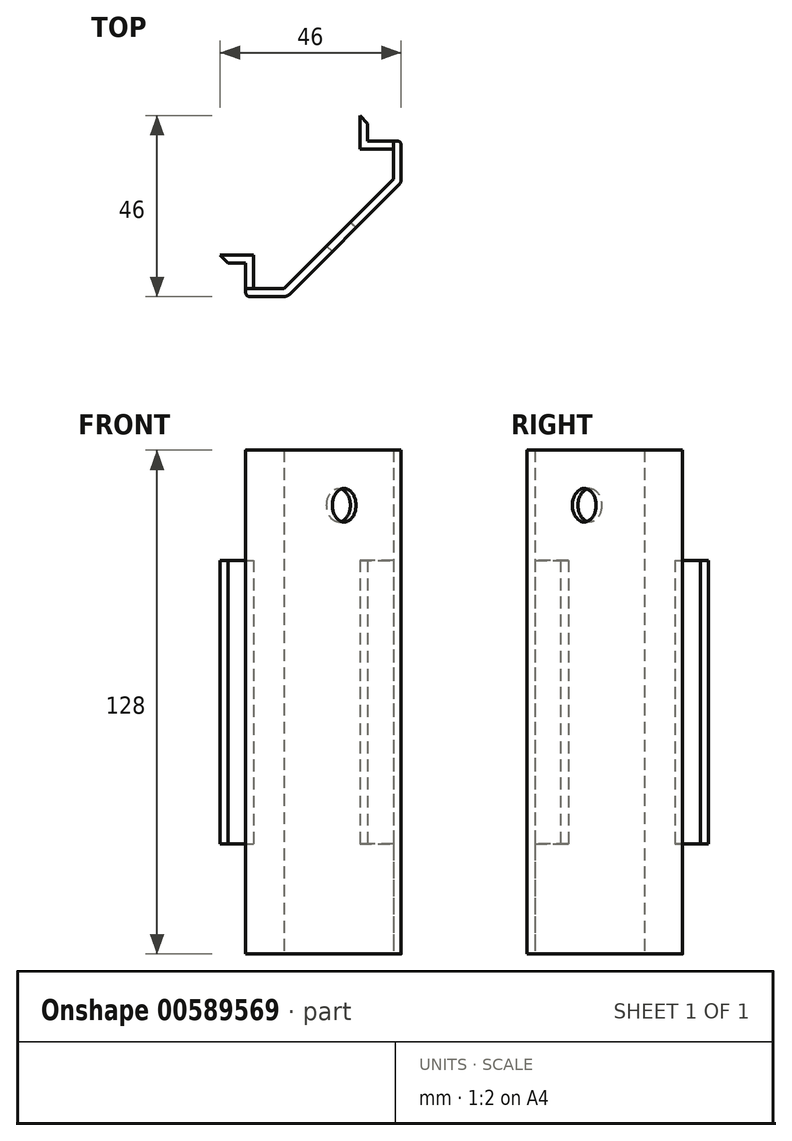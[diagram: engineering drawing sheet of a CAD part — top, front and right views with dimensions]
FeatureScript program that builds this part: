
annotation { "Feature Type Name" : "Feature", "Feature Type Description" : "" }
export const myFeature = defineFeature(function(context is Context, id is Id, definition is map)
    precondition{}
    {
        {
            var Q0;
            Q0=qCreatedBy(makeId("Top.planeOp"),FACE);
            var sketch = newSketch(context, id + "F0", { "sketchPlane" : qUnion([Q0])});
            skLineSegment(sketch, "E0", {"start": v(-68.1, 0) * mm, "end": v(72.16, 0) * mm, "construction": true});
            skLineSegment(sketch, "E1", {"start": v(0, 70.28) * mm, "end": v(0, -61.88) * mm, "construction": true});
            skLineSegment(sketch, "E2.bottom", {"start": v(-19.75, 19.75) * mm, "end": v(19.75, 19.75) * mm, "construction": true});
            skLineSegment(sketch, "E2.top", {"start": v(-19.75, -19.75) * mm, "end": v(19.75, -19.75) * mm, "construction": true});
            skLineSegment(sketch, "E2.left", {"start": v(-19.75, 19.75) * mm, "end": v(-19.75, -19.75) * mm, "construction": true});
            skLineSegment(sketch, "E2.right", {"start": v(19.75, 19.75) * mm, "end": v(19.75, -19.75) * mm, "construction": true});
            skLineSegment(sketch, "E3", {"start": v(-19.75, -19.75) * mm, "end": v(-9.25, -19.75) * mm});
            skLineSegment(sketch, "E4", {"start": v(19.75, 19.75) * mm, "end": v(19.75, 9.25) * mm});
            skLineSegment(sketch, "E5", {"start": v(-9.25, -19.75) * mm, "end": v(19.75, 9.25) * mm});
            skLineSegment(sketch, "E6.0", {"start": v(-19.75, -17.75) * mm, "end": v(-10.08, -17.75) * mm});
            skLineSegment(sketch, "E6.1", {"start": v(-10.08, -17.75) * mm, "end": v(17.75, 10.08) * mm});
            skLineSegment(sketch, "E6.2", {"start": v(17.75, 19.75) * mm, "end": v(17.75, 10.08) * mm});
            skLineSegment(sketch, "E7", {"start": v(-19.75, -19.75) * mm, "end": v(-19.75, -17.75) * mm});
            skLineSegment(sketch, "E8", {"start": v(19.75, 19.75) * mm, "end": v(17.75, 19.75) * mm});
            skSolve(sketch);
        }
        {
            var Q0;
            Q0=qSketchRegion(id+"F0",true);
            extrude(context, id + "F1", {"entities" : qUnion([Q0]), "depth" : 28 * mm, "offsetDistance" : 25 * mm});
        }
        {
            var Q0;
            Q0=makeQuery(id+"F1.opExtrude","CAP_FACE",FACE,{"disambiguationData":[OSD([sQuery(id+"F0.wireOp",EDGE,"E3"),sQuery(id+"F0.wireOp",EDGE,"E4"),sQuery(id+"F0.wireOp",EDGE,"E5"),sQuery(id+"F0.wireOp",EDGE,"E6.0"),sQuery(id+"F0.wireOp",EDGE,"E6.1"),sQuery(id+"F0.wireOp",EDGE,"E6.2"),sQuery(id+"F0.wireOp",EDGE,"E7"),sQuery(id+"F0.wireOp",EDGE,"E8")])],"isStart":false});
            var sketch = newSketch(context, id + "F2", { "sketchPlane" : qUnion([Q0])});
            skLineSegment(sketch, "E9.1", {"start": v(-9.25, -19.75) * mm, "end": v(19.75, 9.25) * mm});
            skLineSegment(sketch, "E9.2", {"start": v(19.75, 19.75) * mm, "end": v(19.75, 9.25) * mm});
            skLineSegment(sketch, "E10", {"start": v(19.75, 19.75) * mm, "end": v(11.25, 19.75) * mm});
            skLineSegment(sketch, "E11", {"start": v(17.75, 17.75) * mm, "end": v(17.75, 10.08) * mm});
            skLineSegment(sketch, "E12", {"start": v(17.75, 10.08) * mm, "end": v(16.59, 8.91) * mm});
            skLineSegment(sketch, "E13.left", {"start": v(11.25, 19.75) * mm, "end": v(11.25, 24.25) * mm});
            skLineSegment(sketch, "E14", {"start": v(11.25, 24.25) * mm, "end": v(9.25, 26.25) * mm});
            skLineSegment(sketch, "E15.trimOffspring", {"start": v(16.59, 8.91) * mm, "end": v(-8.91, -16.59) * mm});
            skLineSegment(sketch, "E16.0", {"start": v(9.25, 19.75) * mm, "end": v(9.25, 23.42) * mm});
            skLineSegment(sketch, "E17.0", {"start": v(9.25, 23.42) * mm, "end": v(9.25, 23.42) * mm});
            skLineSegment(sketch, "E18.trimOffspring", {"start": v(9.25, 23.42) * mm, "end": v(9.25, 26.25) * mm});
            skLineSegment(sketch, "E19", {"start": v(0, 0) * mm, "end": v(5.25, -5.25) * mm, "construction": true});
            skLineSegment(sketch, "E20.MirrorCS", {"start": v(-19.75, -9.25) * mm, "end": v(-23.42, -9.25) * mm});
            skLineSegment(sketch, "E21.MirrorCS", {"start": v(-19.75, -11.25) * mm, "end": v(-24.25, -11.25) * mm});
            skLineSegment(sketch, "E22.MirrorCS", {"start": v(-23.42, -9.25) * mm, "end": v(-26.25, -9.25) * mm});
            skLineSegment(sketch, "E23.MirrorCS", {"start": v(-19.75, -19.75) * mm, "end": v(-9.25, -19.75) * mm});
            skLineSegment(sketch, "E24.MirrorCS", {"start": v(-10.08, -17.75) * mm, "end": v(-8.91, -16.59) * mm});
            skLineSegment(sketch, "E25.MirrorCS", {"start": v(-24.25, -11.25) * mm, "end": v(-26.25, -9.25) * mm});
            skLineSegment(sketch, "E26.MirrorCS", {"start": v(-17.75, -17.75) * mm, "end": v(-10.08, -17.75) * mm});
            skLineSegment(sketch, "E27.MirrorCS", {"start": v(-23.42, -9.25) * mm, "end": v(-23.42, -9.25) * mm});
            skLineSegment(sketch, "E28.MirrorCS", {"start": v(-19.75, -19.75) * mm, "end": v(-19.75, -11.25) * mm});
            skLineSegment(sketch, "E29.trimOffspring", {"start": v(-8.91, -16.59) * mm, "end": v(-10.08, -17.75) * mm});
            skLineSegment(sketch, "E30", {"start": v(9.25, 19.75) * mm, "end": v(9.25, 17.75) * mm});
            skLineSegment(sketch, "E31", {"start": v(9.25, 17.75) * mm, "end": v(17.75, 17.75) * mm});
            skLineSegment(sketch, "E32", {"start": v(-19.75, -9.25) * mm, "end": v(-17.75, -9.25) * mm});
            skLineSegment(sketch, "E33", {"start": v(-17.75, -9.25) * mm, "end": v(-17.75, -17.75) * mm});
            skSolve(sketch);
        }
        {
            var Q0;
            Q0=qSketchRegion(id+"F2",true);
            extrude(context, id + "F3", {"entities" : qUnion([Q0]), "operationType" : NewBodyOperationType.ADD, "depth" : 72 * mm, "offsetDistance" : 25 * mm});
        }
        {
            var Q0;
            Q0=makeQuery(id+"F3.opExtrude","CAP_FACE",FACE,{"disambiguationData":[OSD([sQuery(id+"F2.wireOp",EDGE,"E9.1"),sQuery(id+"F2.wireOp",EDGE,"E9.2"),sQuery(id+"F2.wireOp",EDGE,"E10"),sQuery(id+"F2.wireOp",EDGE,"E11"),sQuery(id+"F2.wireOp",EDGE,"E12"),sQuery(id+"F2.wireOp",EDGE,"E13.left"),sQuery(id+"F2.wireOp",EDGE,"E14"),sQuery(id+"F2.wireOp",EDGE,"E15.trimOffspring"),sQuery(id+"F2.wireOp",EDGE,"E16.0"),sQuery(id+"F2.wireOp",EDGE,"E17.0"),sQuery(id+"F2.wireOp",EDGE,"E18.trimOffspring"),sQuery(id+"F2.wireOp",EDGE,"E20.MirrorCS"),sQuery(id+"F2.wireOp",EDGE,"E21.MirrorCS"),sQuery(id+"F2.wireOp",EDGE,"E22.MirrorCS"),sQuery(id+"F2.wireOp",EDGE,"E23.MirrorCS"),sQuery(id+"F2.wireOp",EDGE,"E25.MirrorCS"),sQuery(id+"F2.wireOp",EDGE,"E26.MirrorCS"),sQuery(id+"F2.wireOp",EDGE,"E27.MirrorCS"),sQuery(id+"F2.wireOp",EDGE,"E28.MirrorCS"),sQuery(id+"F2.wireOp",EDGE,"E29.trimOffspring"),sQuery(id+"F2.wireOp",EDGE,"E30"),sQuery(id+"F2.wireOp",EDGE,"E31"),sQuery(id+"F2.wireOp",EDGE,"E32"),sQuery(id+"F2.wireOp",EDGE,"E33")])],"isStart":false});
            var sketch = newSketch(context, id + "F4", { "sketchPlane" : qUnion([Q0])});
            skLineSegment(sketch, "E34.0.0", {"start": v(19.75, 19.75) * mm, "end": v(19.75, 9.25) * mm});
            skLineSegment(sketch, "E34.0.1", {"start": v(19.75, 9.25) * mm, "end": v(-9.25, -19.75) * mm});
            skLineSegment(sketch, "E34.0.2", {"start": v(-9.25, -19.75) * mm, "end": v(-19.75, -19.75) * mm});
            skLineSegment(sketch, "E34.0.3", {"start": v(-19.75, -19.75) * mm, "end": v(-19.75, -17.75) * mm});
            skLineSegment(sketch, "E34.0.4", {"start": v(-19.75, -17.75) * mm, "end": v(-10.08, -17.75) * mm});
            skLineSegment(sketch, "E34.0.5", {"start": v(-10.08, -17.75) * mm, "end": v(17.75, 10.08) * mm});
            skLineSegment(sketch, "E34.0.6", {"start": v(17.75, 10.08) * mm, "end": v(17.75, 19.75) * mm});
            skLineSegment(sketch, "E34.0.7", {"start": v(17.75, 19.75) * mm, "end": v(19.75, 19.75) * mm});
            skSolve(sketch);
        }
        {
            var Q0;
            Q0=qSketchRegion(id+"F4",true);
            extrude(context, id + "F5", {"entities" : qUnion([Q0]), "operationType" : NewBodyOperationType.ADD, "depth" : 28 * mm});
        }
        {
            var Q0;
            Q0=makeQuery(id+"F5.boolean.opBoolean","MERGE",EDGE,{"derivedFrom":[makeQuery(id+"F3.boolean.opBoolean","MERGE",EDGE,{"derivedFrom":[makeQuery(id+"F1.opExtrude","SWEPT_EDGE",EDGE,{"disambiguationData":[OSD([sQuery(id+"F0.wireOp",EDGE,"E4"),sQuery(id+"F0.wireOp",EDGE,"E5")])]}),makeQuery(id+"F3.opExtrude","SWEPT_EDGE",EDGE,{"disambiguationData":[OSD([sQuery(id+"F2.wireOp",EDGE,"E9.1"),sQuery(id+"F2.wireOp",EDGE,"E9.2")])]})]}),makeQuery(id+"F5.opExtrude","SWEPT_EDGE",EDGE,{"disambiguationData":[OSD([sQuery(id+"F4.wireOp",EDGE,"E34.0.0"),sQuery(id+"F4.wireOp",EDGE,"E34.0.1")])]})]});
            var Q1;
            Q1=makeQuery(id+"F5.boolean.opBoolean","MERGE",EDGE,{"derivedFrom":[makeQuery(id+"F3.boolean.opBoolean","MERGE",EDGE,{"derivedFrom":[makeQuery(id+"F1.opExtrude","SWEPT_EDGE",EDGE,{"disambiguationData":[OSD([sQuery(id+"F0.wireOp",EDGE,"E3"),sQuery(id+"F0.wireOp",EDGE,"E5")])]}),makeQuery(id+"F3.opExtrude","SWEPT_EDGE",EDGE,{"disambiguationData":[OSD([sQuery(id+"F2.wireOp",EDGE,"E9.1"),sQuery(id+"F2.wireOp",EDGE,"E23.MirrorCS")])]})]}),makeQuery(id+"F5.opExtrude","SWEPT_EDGE",EDGE,{"disambiguationData":[OSD([sQuery(id+"F4.wireOp",EDGE,"E34.0.1"),sQuery(id+"F4.wireOp",EDGE,"E34.0.2")])]})]});
            fillet(context, id + "F6", {"entities" : qUnion([Q0, Q1]), "radius" : 2 * mm, "tangentPropagation" : true, "allowEdgeOverflow" : false});
        }
        {
            var Q0;
            Q0=makeQuery(id+"F5.boolean.opBoolean","MERGE",EDGE,{"derivedFrom":[makeQuery(id+"F3.boolean.opBoolean","MERGE",EDGE,{"derivedFrom":[makeQuery(id+"F1.opExtrude","SWEPT_EDGE",EDGE,{"disambiguationData":[OSD([sQuery(id+"F0.wireOp",EDGE,"E3"),sQuery(id+"F0.wireOp",EDGE,"E7")])]}),makeQuery(id+"F3.opExtrude","SWEPT_EDGE",EDGE,{"disambiguationData":[OSD([sQuery(id+"F2.wireOp",EDGE,"E23.MirrorCS"),sQuery(id+"F2.wireOp",EDGE,"E28.MirrorCS")])]})]}),makeQuery(id+"F5.opExtrude","SWEPT_EDGE",EDGE,{"disambiguationData":[OSD([sQuery(id+"F4.wireOp",EDGE,"E34.0.2"),sQuery(id+"F4.wireOp",EDGE,"E34.0.3")])]})]});
            var Q1;
            Q1=makeQuery(id+"F5.boolean.opBoolean","MERGE",EDGE,{"derivedFrom":[makeQuery(id+"F3.boolean.opBoolean","MERGE",EDGE,{"derivedFrom":[makeQuery(id+"F1.opExtrude","SWEPT_EDGE",EDGE,{"disambiguationData":[OSD([sQuery(id+"F0.wireOp",EDGE,"E4"),sQuery(id+"F0.wireOp",EDGE,"E8")])]}),makeQuery(id+"F3.opExtrude","SWEPT_EDGE",EDGE,{"disambiguationData":[OSD([sQuery(id+"F2.wireOp",EDGE,"E9.2"),sQuery(id+"F2.wireOp",EDGE,"E10")])]})]}),makeQuery(id+"F5.opExtrude","SWEPT_EDGE",EDGE,{"disambiguationData":[OSD([sQuery(id+"F4.wireOp",EDGE,"E34.0.0"),sQuery(id+"F4.wireOp",EDGE,"E34.0.7")])]})]});
            fillet(context, id + "F7", {"entities" : qUnion([Q0, Q1]), "radius" : 1 * mm, "tangentPropagation" : true, "allowEdgeOverflow" : false});
        }
        {
            var Q0;
            Q0=makeQuery(id+"F5.boolean.opBoolean","MERGE",FACE,{"derivedFrom":[makeQuery(id+"F3.boolean.opBoolean","MERGE",FACE,{"derivedFrom":[makeQuery(id+"F1.opExtrude","SWEPT_FACE",FACE,{"disambiguationData":[OSD([sQuery(id+"F0.wireOp",EDGE,"E5")])]}),makeQuery(id+"F3.opExtrude","SWEPT_FACE",FACE,{"disambiguationData":[OSD([sQuery(id+"F2.wireOp",EDGE,"E9.1")])]})]}),makeQuery(id+"F5.opExtrude","SWEPT_FACE",FACE,{"disambiguationData":[OSD([sQuery(id+"F4.wireOp",EDGE,"E34.0.1")])]})]});
            var sketch = newSketch(context, id + "F8", { "sketchPlane" : qUnion([Q0])});
            skLineSegment(sketch, "E35.0", {"start": v(-19.1, 100) * mm, "end": v(-25.1, 100) * mm, "construction": true});
            skLineSegment(sketch, "E36", {"start": v(-19.1, 100) * mm, "end": v(27.6, 100) * mm, "construction": true});
            skLineSegment(sketch, "E37", {"start": v(0, 128) * mm, "end": v(0, 100) * mm, "construction": true});
            skCircle(sketch, "E38", {"center": v(0, 114) * mm, "radius": 4.25 * mm});
            skSolve(sketch);
        }
        {
            var Q0;
            Q0=qSketchRegion(id+"F8",true);
            extrude(context, id + "F9", {"entities" : qUnion([Q0]), "operationType" : NewBodyOperationType.REMOVE, "oppositeDirection" : true, "depth" : 25 * mm, "offsetDistance" : 25 * mm});
        }
    });
